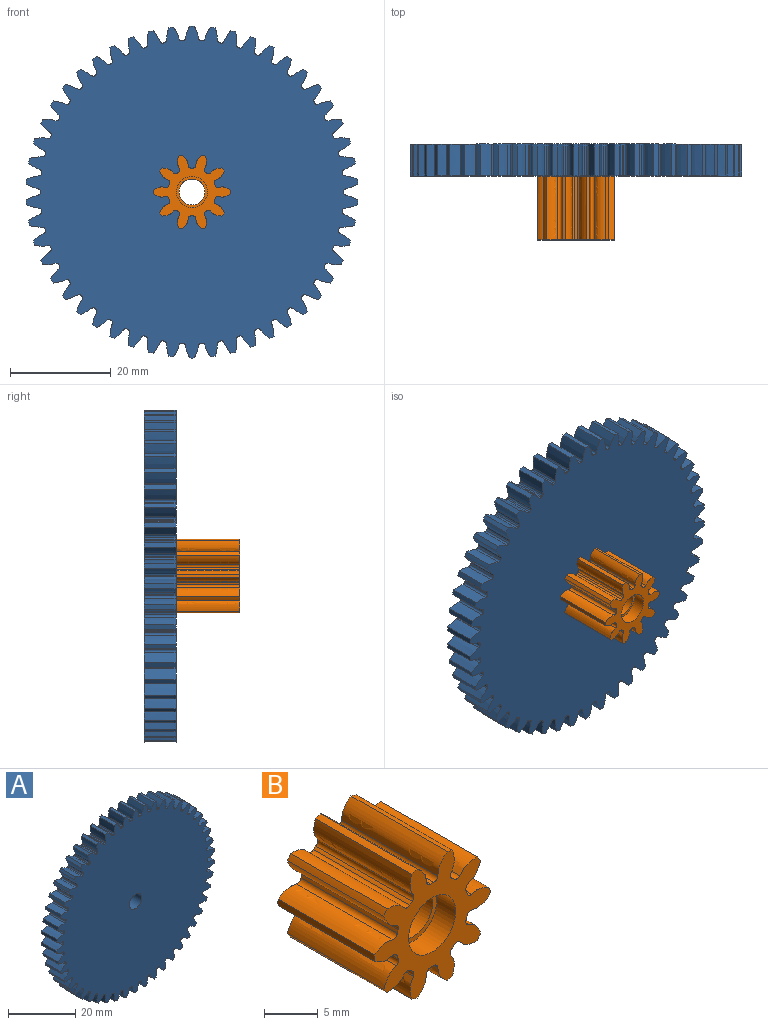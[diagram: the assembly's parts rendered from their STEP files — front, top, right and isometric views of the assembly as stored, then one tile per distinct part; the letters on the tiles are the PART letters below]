
ASSEMBLY  parts=2 mates=1
PART A: 305 faces, bbox 66x6.4x66 mm
  f0: cylinder r=2.59mm len=5.18mm, axis (0,-1,0), area 62.7mm2, adj f50,f303
  f1: cylinder r=33.02mm len=6.35mm, axis (0,1,0), area 6.2mm2, adj f50,f52,f53,f300
  f2: cylinder r=33.02mm len=6.35mm, axis (0,1,0), area 6.2mm2, adj f50,f52,f295,f298
  f3: cylinder r=33.02mm len=6.35mm, axis (0,1,0), area 6.2mm2, adj f50,f52,f290,f293
  f4: cylinder r=33.02mm len=6.35mm, axis (0,1,0), area 6.2mm2, adj f50,f52,f285,f288
  f5: cylinder r=33.02mm len=6.35mm, axis (0,1,0), area 6.2mm2, adj f50,f52,f263,f280
  f6: cylinder r=33.02mm len=6.35mm, axis (0,1,0), area 6.2mm2, adj f50,f52,f275,f278
  f7: cylinder r=33.02mm len=6.35mm, axis (0,1,0), area 6.2mm2, adj f50,f52,f270,f283
  f8: cylinder r=33.02mm len=6.35mm, axis (0,1,0), area 6.2mm2, adj f50,f52,f265,f268
  f9: cylinder r=33.02mm len=6.35mm, axis (0,1,0), area 6.2mm2, adj f50,f52,f260,f273
  f10: cylinder r=33.02mm len=6.35mm, axis (0,1,0), area 6.2mm2, adj f50,f52,f255,f258
  f11: cylinder r=33.02mm len=6.35mm, axis (0,1,0), area 6.2mm2, adj f50,f52,f250,f253
  f12: cylinder r=33.02mm len=6.35mm, axis (0,1,0), area 6.2mm2, adj f50,f52,f245,f248
  f13: cylinder r=33.02mm len=6.35mm, axis (0,1,0), area 6.2mm2, adj f50,f52,f240,f243
  f14: cylinder r=33.02mm len=6.35mm, axis (0,1,0), area 6.2mm2, adj f50,f52,f235,f238
  f15: cylinder r=33.02mm len=6.35mm, axis (0,1,0), area 6.2mm2, adj f50,f52,f230,f233
  f16: cylinder r=33.02mm len=6.35mm, axis (0,1,0), area 6.2mm2, adj f50,f52,f225,f228
  f17: cylinder r=33.02mm len=6.35mm, axis (0,1,0), area 6.2mm2, adj f50,f52,f203,f220
  f18: cylinder r=33.02mm len=6.35mm, axis (0,1,0), area 6.2mm2, adj f50,f52,f215,f218
  f19: cylinder r=33.02mm len=6.35mm, axis (0,1,0), area 6.2mm2, adj f50,f52,f210,f223
  f20: cylinder r=33.02mm len=6.35mm, axis (0,1,0), area 6.2mm2, adj f50,f52,f205,f208
  f21: cylinder r=33.02mm len=6.35mm, axis (0,1,0), area 6.2mm2, adj f50,f52,f200,f213
  f22: cylinder r=33.02mm len=6.35mm, axis (0,1,0), area 6.2mm2, adj f50,f52,f195,f198
  f23: cylinder r=33.02mm len=6.35mm, axis (0,1,0), area 6.2mm2, adj f50,f52,f190,f193
  f24: cylinder r=33.02mm len=6.35mm, axis (0,1,0), area 6.2mm2, adj f50,f52,f185,f188
  f25: cylinder r=33.02mm len=6.35mm, axis (0,1,0), area 6.2mm2, adj f50,f52,f180,f183
  f26: cylinder r=33.02mm len=6.35mm, axis (0,1,0), area 6.2mm2, adj f50,f52,f175,f178
  f27: cylinder r=33.02mm len=6.35mm, axis (0,1,0), area 6.2mm2, adj f50,f52,f170,f173
  f28: cylinder r=33.02mm len=6.35mm, axis (0,1,0), area 6.2mm2, adj f50,f52,f165,f168
  f29: cylinder r=33.02mm len=6.35mm, axis (0,1,0), area 6.2mm2, adj f50,f52,f148,f160
  f30: cylinder r=33.02mm len=6.35mm, axis (0,1,0), area 6.2mm2, adj f50,f52,f155,f158
  f31: cylinder r=33.02mm len=6.35mm, axis (0,1,0), area 6.2mm2, adj f50,f52,f143,f150
  f32: cylinder r=33.02mm len=6.35mm, axis (0,1,0), area 6.2mm2, adj f50,f52,f145,f163
  f33: cylinder r=33.02mm len=6.35mm, axis (0,1,0), area 6.2mm2, adj f50,f52,f140,f153
  f34: cylinder r=33.02mm len=6.35mm, axis (0,1,0), area 6.2mm2, adj f50,f52,f135,f138
  f35: cylinder r=33.02mm len=6.35mm, axis (0,1,0), area 6.2mm2, adj f50,f52,f130,f133
  f36: cylinder r=33.02mm len=6.35mm, axis (0,1,0), area 6.2mm2, adj f50,f52,f125,f128
  f37: cylinder r=33.02mm len=6.35mm, axis (0,1,0), area 6.2mm2, adj f50,f52,f120,f123
  f38: cylinder r=33.02mm len=6.35mm, axis (0,1,0), area 6.2mm2, adj f50,f52,f115,f118
  f39: cylinder r=33.02mm len=6.35mm, axis (0,1,0), area 6.2mm2, adj f50,f52,f110,f113
  f40: cylinder r=33.02mm len=6.35mm, axis (0,1,0), area 6.2mm2, adj f50,f52,f105,f108
  f41: cylinder r=33.02mm len=6.35mm, axis (0,1,0), area 6.2mm2, adj f50,f52,f93,f100
  f42: cylinder r=33.02mm len=6.35mm, axis (0,1,0), area 6.2mm2, adj f50,f52,f88,f95
  f43: cylinder r=33.02mm len=6.35mm, axis (0,1,0), area 6.2mm2, adj f50,f52,f83,f90
  f44: cylinder r=33.02mm len=6.35mm, axis (0,1,0), area 6.2mm2, adj f50,f52,f68,f85
  f45: cylinder r=33.02mm len=6.35mm, axis (0,1,0), area 6.2mm2, adj f50,f52,f80,f103
  f46: cylinder r=33.02mm len=6.35mm, axis (0,1,0), area 6.2mm2, adj f50,f52,f75,f78
  f47: cylinder r=33.02mm len=6.35mm, axis (0,1,0), area 6.2mm2, adj f50,f52,f63,f70
  f48: cylinder r=33.02mm len=6.35mm, axis (0,1,0), area 6.2mm2, adj f50,f52,f65,f73
  f49: cylinder r=33.02mm len=6.35mm, axis (0,1,0), area 6.2mm2, adj f50,f52,f60,f98
  f50: plane 66.04x65.97mm, normal (0,-1,0), area 3128.1mm2, adj f0,f1,f2,f3,f4,f5,f6,f7
  f51: cylinder r=33.02mm len=6.35mm, axis (0,1,0), area 6.2mm2, adj f50,f52,f55,f58
  f52: plane 66.04x65.97mm, normal (0,1,0), area 3119mm2, adj f1,f2,f3,f4,f5,f6,f7,f8
  f53: extruded ~6.35x2.48mm, area 17mm2, adj f1,f50,f52,f56
  f54: cylinder r=30.16mm len=6.35mm, axis (0,1,0), area 2.2mm2, adj f50,f52,f56,f57
  f55: extruded ~6.35x2.48mm, area 17mm2, adj f50,f51,f52,f57
  f56: cylinder r=0.44mm len=6.35mm, axis (0,1,0), area 3.8mm2, adj f50,f52,f53,f54
  f57: cylinder r=0.44mm len=6.35mm, axis (0,1,0), area 3.8mm2, adj f50,f52,f54,f55
  f58: extruded ~6.35x2.58mm, area 17mm2, adj f50,f51,f52,f61
  f59: cylinder r=30.16mm len=6.35mm, axis (0,1,0), area 2.2mm2, adj f50,f52,f61,f62
  f60: extruded ~6.35x2.34mm, area 17mm2, adj f49,f50,f52,f62
  f61: cylinder r=0.44mm len=6.35mm, axis (0,1,0), area 3.8mm2, adj f50,f52,f58,f59
  f62: cylinder r=0.44mm len=6.35mm, axis (0,1,0), area 3.8mm2, adj f50,f52,f59,f60
  f63: extruded ~6.35x2.34mm, area 17mm2, adj f47,f50,f52,f66
  f64: cylinder r=30.16mm len=6.35mm, axis (0,1,0), area 2.2mm2, adj f50,f52,f66,f67
  f65: extruded ~6.35x2.54mm, area 17mm2, adj f48,f50,f52,f67
  f66: cylinder r=0.44mm len=6.35mm, axis (0,1,0), area 3.8mm2, adj f50,f52,f63,f64
  f67: cylinder r=0.44mm len=6.35mm, axis (0,1,0), area 3.8mm2, adj f50,f52,f64,f65
  f68: extruded ~6.35x2.48mm, area 17mm2, adj f44,f50,f52,f71
  f69: cylinder r=30.16mm len=6.35mm, axis (0,1,0), area 2.2mm2, adj f50,f52,f71,f72
  f70: extruded ~6.35x2.42mm, area 17mm2, adj f47,f50,f52,f72
  f71: cylinder r=0.44mm len=6.35mm, axis (0,1,0), area 3.8mm2, adj f50,f52,f68,f69
  f72: cylinder r=0.44mm len=6.35mm, axis (0,1,0), area 3.8mm2, adj f50,f52,f69,f70
  f73: extruded ~6.35x2.16mm, area 17mm2, adj f48,f50,f52,f76
  f74: cylinder r=30.16mm len=6.35mm, axis (0,1,0), area 2.2mm2, adj f50,f52,f76,f77
  f75: extruded ~6.35x2.62mm, area 17mm2, adj f46,f50,f52,f77
  f76: cylinder r=0.44mm len=6.35mm, axis (0,1,0), area 3.8mm2, adj f50,f52,f73,f74
  f77: cylinder r=0.44mm len=6.35mm, axis (0,1,0), area 3.8mm2, adj f50,f52,f74,f75
  f78: extruded ~6.35x1.95mm, area 17mm2, adj f46,f50,f52,f81
  f79: cylinder r=30.16mm len=6.35mm, axis (0,1,0), area 2.2mm2, adj f50,f52,f81,f82
  f80: extruded ~6.35x2.66mm, area 17mm2, adj f45,f50,f52,f82
  f81: cylinder r=0.44mm len=6.35mm, axis (0,1,0), area 3.8mm2, adj f50,f52,f78,f79
  f82: cylinder r=0.44mm len=6.35mm, axis (0,1,0), area 3.8mm2, adj f50,f52,f79,f80
  f83: extruded ~6.35x2.59mm, area 17mm2, adj f43,f50,f52,f86
  f84: cylinder r=30.16mm len=6.35mm, axis (0,1,0), area 2.2mm2, adj f50,f52,f86,f87
  f85: extruded ~6.35x2.25mm, area 17mm2, adj f44,f50,f52,f87
  f86: cylinder r=0.44mm len=6.35mm, axis (0,1,0), area 3.8mm2, adj f50,f52,f83,f84
  f87: cylinder r=0.44mm len=6.35mm, axis (0,1,0), area 3.8mm2, adj f50,f52,f84,f85
  f88: extruded ~6.35x2.65mm, area 17mm2, adj f42,f50,f52,f91
  f89: cylinder r=30.16mm len=6.35mm, axis (0,1,0), area 2.2mm2, adj f50,f52,f91,f92
  f90: extruded ~6.35x2.06mm, area 17mm2, adj f43,f50,f52,f92
  f91: cylinder r=0.44mm len=6.35mm, axis (0,1,0), area 3.8mm2, adj f50,f52,f88,f89
  f92: cylinder r=0.44mm len=6.35mm, axis (0,1,0), area 3.8mm2, adj f50,f52,f89,f90
  f93: extruded ~6.35x2.67mm, area 17mm2, adj f41,f50,f52,f96
  f94: cylinder r=30.16mm len=6.35mm, axis (0,1,0), area 2.2mm2, adj f50,f52,f96,f97
  f95: extruded ~6.35x1.94mm, area 17mm2, adj f42,f50,f52,f97
  f96: cylinder r=0.44mm len=6.35mm, axis (0,1,0), area 3.8mm2, adj f50,f52,f93,f94
  f97: cylinder r=0.44mm len=6.35mm, axis (0,1,0), area 3.8mm2, adj f50,f52,f94,f95
  f98: extruded ~6.35x2.65mm, area 17mm2, adj f49,f50,f52,f101
  f99: cylinder r=30.16mm len=6.35mm, axis (0,1,0), area 2.2mm2, adj f50,f52,f101,f102
  f100: extruded ~6.35x2.16mm, area 17mm2, adj f41,f50,f52,f102
  f101: cylinder r=0.44mm len=6.35mm, axis (0,1,0), area 3.8mm2, adj f50,f52,f98,f99
  f102: cylinder r=0.44mm len=6.35mm, axis (0,1,0), area 3.8mm2, adj f50,f52,f99,f100
  f103: extruded ~6.35x2.06mm, area 17mm2, adj f45,f50,f52,f106
  f104: cylinder r=30.16mm len=6.35mm, axis (0,1,0), area 2.2mm2, adj f50,f52,f106,f107
  f105: extruded ~6.35x2.66mm, area 17mm2, adj f40,f50,f52,f107
  f106: cylinder r=0.44mm len=6.35mm, axis (0,1,0), area 3.8mm2, adj f50,f52,f103,f104
  f107: cylinder r=0.44mm len=6.35mm, axis (0,1,0), area 3.8mm2, adj f50,f52,f104,f105
  f108: extruded ~6.35x2.25mm, area 17mm2, adj f40,f50,f52,f111
  f109: cylinder r=30.16mm len=6.35mm, axis (0,1,0), area 2.2mm2, adj f50,f52,f111,f112
  f110: extruded ~6.35x2.62mm, area 17mm2, adj f39,f50,f52,f112
  f111: cylinder r=0.44mm len=6.35mm, axis (0,1,0), area 3.8mm2, adj f50,f52,f108,f109
  f112: cylinder r=0.44mm len=6.35mm, axis (0,1,0), area 3.8mm2, adj f50,f52,f109,f110
  f113: extruded ~6.35x2.41mm, area 17mm2, adj f39,f50,f52,f116
  f114: cylinder r=30.16mm len=6.35mm, axis (0,1,0), area 2.2mm2, adj f50,f52,f116,f117
  f115: extruded ~6.35x2.54mm, area 17mm2, adj f38,f50,f52,f117
  f116: cylinder r=0.44mm len=6.35mm, axis (0,1,0), area 3.8mm2, adj f50,f52,f113,f114
  f117: cylinder r=0.44mm len=6.35mm, axis (0,1,0), area 3.8mm2, adj f50,f52,f114,f115
  f118: extruded ~6.35x2.54mm, area 17mm2, adj f38,f50,f52,f121
  f119: cylinder r=30.16mm len=6.35mm, axis (0,1,0), area 2.2mm2, adj f50,f52,f121,f122
  f120: extruded ~6.35x2.41mm, area 17mm2, adj f37,f50,f52,f122
  f121: cylinder r=0.44mm len=6.35mm, axis (0,1,0), area 3.8mm2, adj f50,f52,f118,f119
  f122: cylinder r=0.44mm len=6.35mm, axis (0,1,0), area 3.8mm2, adj f50,f52,f119,f120
  f123: extruded ~6.35x2.62mm, area 17mm2, adj f37,f50,f52,f126
  f124: cylinder r=30.16mm len=6.35mm, axis (0,1,0), area 2.2mm2, adj f50,f52,f126,f127
  f125: extruded ~6.35x2.25mm, area 17mm2, adj f36,f50,f52,f127
  f126: cylinder r=0.44mm len=6.35mm, axis (0,1,0), area 3.8mm2, adj f50,f52,f123,f124
  f127: cylinder r=0.44mm len=6.35mm, axis (0,1,0), area 3.8mm2, adj f50,f52,f124,f125
  f128: extruded ~6.35x2.66mm, area 17mm2, adj f36,f50,f52,f131
  f129: cylinder r=30.16mm len=6.35mm, axis (0,1,0), area 2.2mm2, adj f50,f52,f131,f132
  f130: extruded ~6.35x2.06mm, area 17mm2, adj f35,f50,f52,f132
  f131: cylinder r=0.44mm len=6.35mm, axis (0,1,0), area 3.8mm2, adj f50,f52,f128,f129
  f132: cylinder r=0.44mm len=6.35mm, axis (0,1,0), area 3.8mm2, adj f50,f52,f129,f130
  f133: extruded ~6.35x2.66mm, area 17mm2, adj f35,f50,f52,f136
  f134: cylinder r=30.16mm len=6.35mm, axis (0,1,0), area 2.2mm2, adj f50,f52,f136,f137
  f135: extruded ~6.35x1.95mm, area 17mm2, adj f34,f50,f52,f137
  f136: cylinder r=0.44mm len=6.35mm, axis (0,1,0), area 3.8mm2, adj f50,f52,f133,f134
  f137: cylinder r=0.44mm len=6.35mm, axis (0,1,0), area 3.8mm2, adj f50,f52,f134,f135
  f138: extruded ~6.35x2.62mm, area 17mm2, adj f34,f50,f52,f141
  f139: cylinder r=30.16mm len=6.35mm, axis (0,1,0), area 2.2mm2, adj f50,f52,f141,f142
  f140: extruded ~6.35x2.16mm, area 17mm2, adj f33,f50,f52,f142
  f141: cylinder r=0.44mm len=6.35mm, axis (0,1,0), area 3.8mm2, adj f50,f52,f138,f139
  f142: cylinder r=0.44mm len=6.35mm, axis (0,1,0), area 3.8mm2, adj f50,f52,f139,f140
  f143: extruded ~6.35x2.06mm, area 17mm2, adj f31,f50,f52,f146
  f144: cylinder r=30.16mm len=6.35mm, axis (0,1,0), area 2.2mm2, adj f50,f52,f146,f147
  f145: extruded ~6.35x2.65mm, area 17mm2, adj f32,f50,f52,f147
  f146: cylinder r=0.44mm len=6.35mm, axis (0,1,0), area 3.8mm2, adj f50,f52,f143,f144
  f147: cylinder r=0.44mm len=6.35mm, axis (0,1,0), area 3.8mm2, adj f50,f52,f144,f145
  f148: extruded ~6.35x2.25mm, area 17mm2, adj f29,f50,f52,f151
  f149: cylinder r=30.16mm len=6.35mm, axis (0,1,0), area 2.2mm2, adj f50,f52,f151,f152
  f150: extruded ~6.35x2.59mm, area 17mm2, adj f31,f50,f52,f152
  f151: cylinder r=0.44mm len=6.35mm, axis (0,1,0), area 3.8mm2, adj f50,f52,f148,f149
  f152: cylinder r=0.44mm len=6.35mm, axis (0,1,0), area 3.8mm2, adj f50,f52,f149,f150
  f153: extruded ~6.35x2.54mm, area 17mm2, adj f33,f50,f52,f156
  f154: cylinder r=30.16mm len=6.35mm, axis (0,1,0), area 2.2mm2, adj f50,f52,f156,f157
  f155: extruded ~6.35x2.34mm, area 17mm2, adj f30,f50,f52,f157
  f156: cylinder r=0.44mm len=6.35mm, axis (0,1,0), area 3.8mm2, adj f50,f52,f153,f154
  f157: cylinder r=0.44mm len=6.35mm, axis (0,1,0), area 3.8mm2, adj f50,f52,f154,f155
  f158: extruded ~6.35x2.42mm, area 17mm2, adj f30,f50,f52,f161
  f159: cylinder r=30.16mm len=6.35mm, axis (0,1,0), area 2.2mm2, adj f50,f52,f161,f162
  f160: extruded ~6.35x2.48mm, area 17mm2, adj f29,f50,f52,f162
  f161: cylinder r=0.44mm len=6.35mm, axis (0,1,0), area 3.8mm2, adj f50,f52,f158,f159
  f162: cylinder r=0.44mm len=6.35mm, axis (0,1,0), area 3.8mm2, adj f50,f52,f159,f160
  f163: extruded ~6.35x1.94mm, area 17mm2, adj f32,f50,f52,f166
  f164: cylinder r=30.16mm len=6.35mm, axis (0,1,0), area 2.2mm2, adj f50,f52,f166,f167
  f165: extruded ~6.35x2.67mm, area 17mm2, adj f28,f50,f52,f167
  f166: cylinder r=0.44mm len=6.35mm, axis (0,1,0), area 3.8mm2, adj f50,f52,f163,f164
  f167: cylinder r=0.44mm len=6.35mm, axis (0,1,0), area 3.8mm2, adj f50,f52,f164,f165
  f168: extruded ~6.35x2.16mm, area 17mm2, adj f28,f50,f52,f171
  f169: cylinder r=30.16mm len=6.35mm, axis (0,1,0), area 2.2mm2, adj f50,f52,f171,f172
  f170: extruded ~6.35x2.65mm, area 17mm2, adj f27,f50,f52,f172
  f171: cylinder r=0.44mm len=6.35mm, axis (0,1,0), area 3.8mm2, adj f50,f52,f168,f169
  f172: cylinder r=0.44mm len=6.35mm, axis (0,1,0), area 3.8mm2, adj f50,f52,f169,f170
  f173: extruded ~6.35x2.34mm, area 17mm2, adj f27,f50,f52,f176
  f174: cylinder r=30.16mm len=6.35mm, axis (0,1,0), area 2.2mm2, adj f50,f52,f176,f177
  f175: extruded ~6.35x2.58mm, area 17mm2, adj f26,f50,f52,f177
  f176: cylinder r=0.44mm len=6.35mm, axis (0,1,0), area 3.8mm2, adj f50,f52,f173,f174
  f177: cylinder r=0.44mm len=6.35mm, axis (0,1,0), area 3.8mm2, adj f50,f52,f174,f175
  f178: extruded ~6.35x2.48mm, area 17mm2, adj f26,f50,f52,f181
  f179: cylinder r=30.16mm len=6.35mm, axis (0,1,0), area 2.2mm2, adj f50,f52,f181,f182
  f180: extruded ~6.35x2.48mm, area 17mm2, adj f25,f50,f52,f182
  f181: cylinder r=0.44mm len=6.35mm, axis (0,1,0), area 3.8mm2, adj f50,f52,f178,f179
  f182: cylinder r=0.44mm len=6.35mm, axis (0,1,0), area 3.8mm2, adj f50,f52,f179,f180
  f183: extruded ~6.35x2.58mm, area 17mm2, adj f25,f50,f52,f186
  f184: cylinder r=30.16mm len=6.35mm, axis (0,1,0), area 2.2mm2, adj f50,f52,f186,f187
  f185: extruded ~6.35x2.34mm, area 17mm2, adj f24,f50,f52,f187
  f186: cylinder r=0.44mm len=6.35mm, axis (0,1,0), area 3.8mm2, adj f50,f52,f183,f184
  f187: cylinder r=0.44mm len=6.35mm, axis (0,1,0), area 3.8mm2, adj f50,f52,f184,f185
  f188: extruded ~6.35x2.65mm, area 17mm2, adj f24,f50,f52,f191
  f189: cylinder r=30.16mm len=6.35mm, axis (0,1,0), area 2.2mm2, adj f50,f52,f191,f192
  f190: extruded ~6.35x2.16mm, area 17mm2, adj f23,f50,f52,f192
  f191: cylinder r=0.44mm len=6.35mm, axis (0,1,0), area 3.8mm2, adj f50,f52,f188,f189
  f192: cylinder r=0.44mm len=6.35mm, axis (0,1,0), area 3.8mm2, adj f50,f52,f189,f190
  f193: extruded ~6.35x2.67mm, area 17mm2, adj f23,f50,f52,f196
  f194: cylinder r=30.16mm len=6.35mm, axis (0,1,0), area 2.2mm2, adj f50,f52,f196,f197
  f195: extruded ~6.35x1.94mm, area 17mm2, adj f22,f50,f52,f197
  f196: cylinder r=0.44mm len=6.35mm, axis (0,1,0), area 3.8mm2, adj f50,f52,f193,f194
  f197: cylinder r=0.44mm len=6.35mm, axis (0,1,0), area 3.8mm2, adj f50,f52,f194,f195
  f198: extruded ~6.35x2.65mm, area 17mm2, adj f22,f50,f52,f201
  f199: cylinder r=30.16mm len=6.35mm, axis (0,1,0), area 2.2mm2, adj f50,f52,f201,f202
  f200: extruded ~6.35x2.06mm, area 17mm2, adj f21,f50,f52,f202
  f201: cylinder r=0.44mm len=6.35mm, axis (0,1,0), area 3.8mm2, adj f50,f52,f198,f199
  f202: cylinder r=0.44mm len=6.35mm, axis (0,1,0), area 3.8mm2, adj f50,f52,f199,f200
  f203: extruded ~6.35x2.34mm, area 17mm2, adj f17,f50,f52,f206
  f204: cylinder r=30.16mm len=6.35mm, axis (0,1,0), area 2.2mm2, adj f50,f52,f206,f207
  f205: extruded ~6.35x2.54mm, area 17mm2, adj f20,f50,f52,f207
  f206: cylinder r=0.44mm len=6.35mm, axis (0,1,0), area 3.8mm2, adj f50,f52,f203,f204
  f207: cylinder r=0.44mm len=6.35mm, axis (0,1,0), area 3.8mm2, adj f50,f52,f204,f205
  f208: extruded ~6.35x2.16mm, area 17mm2, adj f20,f50,f52,f211
  f209: cylinder r=30.16mm len=6.35mm, axis (0,1,0), area 2.2mm2, adj f50,f52,f211,f212
  f210: extruded ~6.35x2.62mm, area 17mm2, adj f19,f50,f52,f212
  f211: cylinder r=0.44mm len=6.35mm, axis (0,1,0), area 3.8mm2, adj f50,f52,f208,f209
  f212: cylinder r=0.44mm len=6.35mm, axis (0,1,0), area 3.8mm2, adj f50,f52,f209,f210
  f213: extruded ~6.35x2.59mm, area 17mm2, adj f21,f50,f52,f216
  f214: cylinder r=30.16mm len=6.35mm, axis (0,1,0), area 2.2mm2, adj f50,f52,f216,f217
  f215: extruded ~6.35x2.25mm, area 17mm2, adj f18,f50,f52,f217
  f216: cylinder r=0.44mm len=6.35mm, axis (0,1,0), area 3.8mm2, adj f50,f52,f213,f214
  f217: cylinder r=0.44mm len=6.35mm, axis (0,1,0), area 3.8mm2, adj f50,f52,f214,f215
  f218: extruded ~6.35x2.48mm, area 17mm2, adj f18,f50,f52,f221
  f219: cylinder r=30.16mm len=6.35mm, axis (0,1,0), area 2.2mm2, adj f50,f52,f221,f222
  f220: extruded ~6.35x2.42mm, area 17mm2, adj f17,f50,f52,f222
  f221: cylinder r=0.44mm len=6.35mm, axis (0,1,0), area 3.8mm2, adj f50,f52,f218,f219
  f222: cylinder r=0.44mm len=6.35mm, axis (0,1,0), area 3.8mm2, adj f50,f52,f219,f220
  f223: extruded ~6.35x1.95mm, area 17mm2, adj f19,f50,f52,f226
  f224: cylinder r=30.16mm len=6.35mm, axis (0,1,0), area 2.2mm2, adj f50,f52,f226,f227
  f225: extruded ~6.35x2.66mm, area 17mm2, adj f16,f50,f52,f227
  f226: cylinder r=0.44mm len=6.35mm, axis (0,1,0), area 3.8mm2, adj f50,f52,f223,f224
  f227: cylinder r=0.44mm len=6.35mm, axis (0,1,0), area 3.8mm2, adj f50,f52,f224,f225
  f228: extruded ~6.35x2.06mm, area 17mm2, adj f16,f50,f52,f231
  f229: cylinder r=30.16mm len=6.35mm, axis (0,1,0), area 2.2mm2, adj f50,f52,f231,f232
  f230: extruded ~6.35x2.66mm, area 17mm2, adj f15,f50,f52,f232
  f231: cylinder r=0.44mm len=6.35mm, axis (0,1,0), area 3.8mm2, adj f50,f52,f228,f229
  f232: cylinder r=0.44mm len=6.35mm, axis (0,1,0), area 3.8mm2, adj f50,f52,f229,f230
  f233: extruded ~6.35x2.25mm, area 17mm2, adj f15,f50,f52,f236
  f234: cylinder r=30.16mm len=6.35mm, axis (0,1,0), area 2.2mm2, adj f50,f52,f236,f237
  f235: extruded ~6.35x2.62mm, area 17mm2, adj f14,f50,f52,f237
  f236: cylinder r=0.44mm len=6.35mm, axis (0,1,0), area 3.8mm2, adj f50,f52,f233,f234
  f237: cylinder r=0.44mm len=6.35mm, axis (0,1,0), area 3.8mm2, adj f50,f52,f234,f235
  f238: extruded ~6.35x2.41mm, area 17mm2, adj f14,f50,f52,f241
  f239: cylinder r=30.16mm len=6.35mm, axis (0,1,0), area 2.2mm2, adj f50,f52,f241,f242
  f240: extruded ~6.35x2.54mm, area 17mm2, adj f13,f50,f52,f242
  f241: cylinder r=0.44mm len=6.35mm, axis (0,1,0), area 3.8mm2, adj f50,f52,f238,f239
  f242: cylinder r=0.44mm len=6.35mm, axis (0,1,0), area 3.8mm2, adj f50,f52,f239,f240
  f243: extruded ~6.35x2.54mm, area 17mm2, adj f13,f50,f52,f246
  f244: cylinder r=30.16mm len=6.35mm, axis (0,1,0), area 2.2mm2, adj f50,f52,f246,f247
  f245: extruded ~6.35x2.41mm, area 17mm2, adj f12,f50,f52,f247
  f246: cylinder r=0.44mm len=6.35mm, axis (0,1,0), area 3.8mm2, adj f50,f52,f243,f244
  f247: cylinder r=0.44mm len=6.35mm, axis (0,1,0), area 3.8mm2, adj f50,f52,f244,f245
  f248: extruded ~6.35x2.62mm, area 17mm2, adj f12,f50,f52,f251
  f249: cylinder r=30.16mm len=6.35mm, axis (0,1,0), area 2.2mm2, adj f50,f52,f251,f252
  f250: extruded ~6.35x2.25mm, area 17mm2, adj f11,f50,f52,f252
  f251: cylinder r=0.44mm len=6.35mm, axis (0,1,0), area 3.8mm2, adj f50,f52,f248,f249
  f252: cylinder r=0.44mm len=6.35mm, axis (0,1,0), area 3.8mm2, adj f50,f52,f249,f250
  f253: extruded ~6.35x2.66mm, area 17mm2, adj f11,f50,f52,f256
  f254: cylinder r=30.16mm len=6.35mm, axis (0,1,0), area 2.2mm2, adj f50,f52,f256,f257
  f255: extruded ~6.35x2.06mm, area 17mm2, adj f10,f50,f52,f257
  f256: cylinder r=0.44mm len=6.35mm, axis (0,1,0), area 3.8mm2, adj f50,f52,f253,f254
  f257: cylinder r=0.44mm len=6.35mm, axis (0,1,0), area 3.8mm2, adj f50,f52,f254,f255
  f258: extruded ~6.35x2.66mm, area 17mm2, adj f10,f50,f52,f261
  f259: cylinder r=30.16mm len=6.35mm, axis (0,1,0), area 2.2mm2, adj f50,f52,f261,f262
  f260: extruded ~6.35x1.95mm, area 17mm2, adj f9,f50,f52,f262
  f261: cylinder r=0.44mm len=6.35mm, axis (0,1,0), area 3.8mm2, adj f50,f52,f258,f259
  f262: cylinder r=0.44mm len=6.35mm, axis (0,1,0), area 3.8mm2, adj f50,f52,f259,f260
  f263: extruded ~6.35x2.42mm, area 17mm2, adj f5,f50,f52,f266
  f264: cylinder r=30.16mm len=6.35mm, axis (0,1,0), area 2.2mm2, adj f50,f52,f266,f267
  f265: extruded ~6.35x2.48mm, area 17mm2, adj f8,f50,f52,f267
  f266: cylinder r=0.44mm len=6.35mm, axis (0,1,0), area 3.8mm2, adj f50,f52,f263,f264
  f267: cylinder r=0.44mm len=6.35mm, axis (0,1,0), area 3.8mm2, adj f50,f52,f264,f265
  f268: extruded ~6.35x2.25mm, area 17mm2, adj f8,f50,f52,f271
  f269: cylinder r=30.16mm len=6.35mm, axis (0,1,0), area 2.2mm2, adj f50,f52,f271,f272
  f270: extruded ~6.35x2.59mm, area 17mm2, adj f7,f50,f52,f272
  f271: cylinder r=0.44mm len=6.35mm, axis (0,1,0), area 3.8mm2, adj f50,f52,f268,f269
  f272: cylinder r=0.44mm len=6.35mm, axis (0,1,0), area 3.8mm2, adj f50,f52,f269,f270
  f273: extruded ~6.35x2.62mm, area 17mm2, adj f9,f50,f52,f276
  f274: cylinder r=30.16mm len=6.35mm, axis (0,1,0), area 2.2mm2, adj f50,f52,f276,f277
  f275: extruded ~6.35x2.16mm, area 17mm2, adj f6,f50,f52,f277
  f276: cylinder r=0.44mm len=6.35mm, axis (0,1,0), area 3.8mm2, adj f50,f52,f273,f274
  f277: cylinder r=0.44mm len=6.35mm, axis (0,1,0), area 3.8mm2, adj f50,f52,f274,f275
  f278: extruded ~6.35x2.54mm, area 17mm2, adj f6,f50,f52,f281
  f279: cylinder r=30.16mm len=6.35mm, axis (0,1,0), area 2.2mm2, adj f50,f52,f281,f282
  f280: extruded ~6.35x2.34mm, area 17mm2, adj f5,f50,f52,f282
  f281: cylinder r=0.44mm len=6.35mm, axis (0,1,0), area 3.8mm2, adj f50,f52,f278,f279
  f282: cylinder r=0.44mm len=6.35mm, axis (0,1,0), area 3.8mm2, adj f50,f52,f279,f280
  f283: extruded ~6.35x2.06mm, area 17mm2, adj f7,f50,f52,f286
  f284: cylinder r=30.16mm len=6.35mm, axis (0,1,0), area 2.2mm2, adj f50,f52,f286,f287
  f285: extruded ~6.35x2.65mm, area 17mm2, adj f4,f50,f52,f287
  f286: cylinder r=0.44mm len=6.35mm, axis (0,1,0), area 3.8mm2, adj f50,f52,f283,f284
  f287: cylinder r=0.44mm len=6.35mm, axis (0,1,0), area 3.8mm2, adj f50,f52,f284,f285
  f288: extruded ~6.35x1.94mm, area 17mm2, adj f4,f50,f52,f291
  f289: cylinder r=30.16mm len=6.35mm, axis (0,1,0), area 2.2mm2, adj f50,f52,f291,f292
  f290: extruded ~6.35x2.67mm, area 17mm2, adj f3,f50,f52,f292
  f291: cylinder r=0.44mm len=6.35mm, axis (0,1,0), area 3.8mm2, adj f50,f52,f288,f289
  f292: cylinder r=0.44mm len=6.35mm, axis (0,1,0), area 3.8mm2, adj f50,f52,f289,f290
  f293: extruded ~6.35x2.16mm, area 17mm2, adj f3,f50,f52,f296
  f294: cylinder r=30.16mm len=6.35mm, axis (0,1,0), area 2.2mm2, adj f50,f52,f296,f297
  f295: extruded ~6.35x2.65mm, area 17mm2, adj f2,f50,f52,f297
  f296: cylinder r=0.44mm len=6.35mm, axis (0,1,0), area 3.8mm2, adj f50,f52,f293,f294
  f297: cylinder r=0.44mm len=6.35mm, axis (0,1,0), area 3.8mm2, adj f50,f52,f294,f295
  f298: extruded ~6.35x2.34mm, area 17mm2, adj f2,f50,f52,f301
  f299: cylinder r=30.16mm len=6.35mm, axis (0,1,0), area 2.2mm2, adj f50,f52,f301,f302
  f300: extruded ~6.35x2.58mm, area 17mm2, adj f1,f50,f52,f302
  f301: cylinder r=0.44mm len=6.35mm, axis (0,1,0), area 3.8mm2, adj f50,f52,f298,f299
  f302: cylinder r=0.44mm len=6.35mm, axis (0,1,0), area 3.8mm2, adj f50,f52,f299,f300
  f303: plane 6.2x6.2mm, normal (0,1,0), area 9.1mm2, adj f0,f304
  f304: cylinder r=3.1mm len=6.2mm, axis (0,1,0), area 48.7mm2, adj f52,f303
PART B: 65 faces, bbox 15.3x12.7x14.7 mm
  f0: cylinder r=2.58mm len=10.2mm, axis (0,-1,0), area 165.6mm2, adj f12,f63
  f1: cylinder r=7.62mm len=12.7mm, axis (0,1,0), area 9.5mm2, adj f10,f12,f15,f59
  f2: cylinder r=7.62mm len=12.7mm, axis (0,1,0), area 9.5mm2, adj f10,f12,f54,f60
  f3: cylinder r=7.62mm len=12.7mm, axis (0,1,0), area 9.5mm2, adj f10,f12,f45,f49
  f4: cylinder r=7.62mm len=12.7mm, axis (0,1,0), area 9.5mm2, adj f10,f12,f44,f55
  f5: cylinder r=7.62mm len=12.7mm, axis (0,1,0), area 9.5mm2, adj f10,f12,f35,f39
  f6: cylinder r=7.62mm len=12.7mm, axis (0,1,0), area 9.5mm2, adj f10,f12,f34,f50
  f7: cylinder r=7.62mm len=12.7mm, axis (0,1,0), area 9.5mm2, adj f10,f12,f29,f40
  f8: cylinder r=7.62mm len=12.7mm, axis (0,1,0), area 9.5mm2, adj f10,f12,f24,f30
  f9: cylinder r=7.62mm len=12.7mm, axis (0,1,0), area 9.5mm2, adj f10,f12,f19,f25
  f10: plane 15.27x14.74mm, normal (0,-1,0), area 91mm2, adj f1,f2,f3,f4,f5,f6,f7,f8
  f11: cylinder r=7.62mm len=12.7mm, axis (0,1,0), area 9.5mm2, adj f10,f12,f14,f20
  f12: plane 15.27x14.74mm, normal (0,1,0), area 100.2mm2, adj f0,f1,f2,f3,f4,f5,f6,f7
  f13: cylinder r=4.76mm len=12.7mm, axis (0,1,0), area 5.2mm2, adj f10,f12,f16,f17
  f14: extruded ~12.7x2.43mm, area 32.7mm2, adj f10,f11,f12,f16
  f15: extruded ~12.7x1.86mm, area 32.7mm2, adj f1,f10,f12,f17
  f16: cylinder r=0.52mm len=12.7mm, axis (0,1,0), area 9.8mm2, adj f10,f12,f13,f14
  f17: cylinder r=0.52mm len=12.7mm, axis (0,1,0), area 9.8mm2, adj f10,f12,f13,f15
  f18: cylinder r=4.76mm len=12.7mm, axis (0,1,0), area 5.2mm2, adj f10,f12,f21,f22
  f19: extruded ~12.7x1.86mm, area 32.7mm2, adj f9,f10,f12,f21
  f20: extruded ~12.7x2.43mm, area 32.7mm2, adj f10,f11,f12,f22
  f21: cylinder r=0.52mm len=12.7mm, axis (0,1,0), area 9.8mm2, adj f10,f12,f18,f19
  f22: cylinder r=0.52mm len=12.7mm, axis (0,1,0), area 9.8mm2, adj f10,f12,f18,f20
  f23: cylinder r=4.76mm len=12.7mm, axis (0,1,0), area 5.2mm2, adj f10,f12,f26,f27
  f24: extruded ~12.7x2.47mm, area 32.7mm2, adj f8,f10,f12,f26
  f25: extruded ~12.7x2.28mm, area 32.7mm2, adj f9,f10,f12,f27
  f26: cylinder r=0.52mm len=12.7mm, axis (0,1,0), area 9.8mm2, adj f10,f12,f23,f24
  f27: cylinder r=0.52mm len=12.7mm, axis (0,1,0), area 9.8mm2, adj f10,f12,f23,f25
  f28: cylinder r=4.76mm len=12.7mm, axis (0,1,0), area 5.2mm2, adj f10,f12,f31,f32
  f29: extruded ~12.7x2.15mm, area 32.7mm2, adj f7,f10,f12,f31
  f30: extruded ~12.7x2.15mm, area 32.7mm2, adj f8,f10,f12,f32
  f31: cylinder r=0.52mm len=12.7mm, axis (0,1,0), area 9.8mm2, adj f10,f12,f28,f29
  f32: cylinder r=0.52mm len=12.7mm, axis (0,1,0), area 9.8mm2, adj f10,f12,f28,f30
  f33: cylinder r=4.76mm len=12.7mm, axis (0,1,0), area 5.2mm2, adj f10,f12,f36,f37
  f34: extruded ~12.7x2.43mm, area 32.7mm2, adj f6,f10,f12,f36
  f35: extruded ~12.7x1.86mm, area 32.7mm2, adj f5,f10,f12,f37
  f36: cylinder r=0.52mm len=12.7mm, axis (0,1,0), area 9.8mm2, adj f10,f12,f33,f34
  f37: cylinder r=0.52mm len=12.7mm, axis (0,1,0), area 9.8mm2, adj f10,f12,f33,f35
  f38: cylinder r=4.76mm len=12.7mm, axis (0,1,0), area 5.2mm2, adj f10,f12,f41,f42
  f39: extruded ~12.7x2.28mm, area 32.7mm2, adj f5,f10,f12,f41
  f40: extruded ~12.7x2.47mm, area 32.7mm2, adj f7,f10,f12,f42
  f41: cylinder r=0.52mm len=12.7mm, axis (0,1,0), area 9.8mm2, adj f10,f12,f38,f39
  f42: cylinder r=0.52mm len=12.7mm, axis (0,1,0), area 9.8mm2, adj f10,f12,f38,f40
  f43: cylinder r=4.76mm len=12.7mm, axis (0,1,0), area 5.2mm2, adj f10,f12,f46,f47
  f44: extruded ~12.7x2.47mm, area 32.7mm2, adj f4,f10,f12,f46
  f45: extruded ~12.7x2.28mm, area 32.7mm2, adj f3,f10,f12,f47
  f46: cylinder r=0.52mm len=12.7mm, axis (0,1,0), area 9.8mm2, adj f10,f12,f43,f44
  f47: cylinder r=0.52mm len=12.7mm, axis (0,1,0), area 9.8mm2, adj f10,f12,f43,f45
  f48: cylinder r=4.76mm len=12.7mm, axis (0,1,0), area 5.2mm2, adj f10,f12,f51,f52
  f49: extruded ~12.7x1.86mm, area 32.7mm2, adj f3,f10,f12,f51
  f50: extruded ~12.7x2.43mm, area 32.7mm2, adj f6,f10,f12,f52
  f51: cylinder r=0.52mm len=12.7mm, axis (0,1,0), area 9.8mm2, adj f10,f12,f48,f49
  f52: cylinder r=0.52mm len=12.7mm, axis (0,1,0), area 9.8mm2, adj f10,f12,f48,f50
  f53: cylinder r=4.76mm len=12.7mm, axis (0,1,0), area 5.2mm2, adj f10,f12,f56,f57
  f54: extruded ~12.7x2.15mm, area 32.7mm2, adj f2,f10,f12,f56
  f55: extruded ~12.7x2.15mm, area 32.7mm2, adj f4,f10,f12,f57
  f56: cylinder r=0.52mm len=12.7mm, axis (0,1,0), area 9.8mm2, adj f10,f12,f53,f54
  f57: cylinder r=0.52mm len=12.7mm, axis (0,1,0), area 9.8mm2, adj f10,f12,f53,f55
  f58: cylinder r=4.76mm len=12.7mm, axis (0,1,0), area 5.2mm2, adj f10,f12,f61,f62
  f59: extruded ~12.7x2.28mm, area 32.7mm2, adj f1,f10,f12,f61
  f60: extruded ~12.7x2.47mm, area 32.7mm2, adj f2,f10,f12,f62
  f61: cylinder r=0.52mm len=12.7mm, axis (0,1,0), area 9.8mm2, adj f10,f12,f58,f59
  f62: cylinder r=0.52mm len=12.7mm, axis (0,1,0), area 9.8mm2, adj f10,f12,f58,f60
  f63: plane 6.2x6.2mm, normal (0,-1,0), area 9.2mm2, adj f0,f64
  f64: cylinder r=3.1mm len=6.2mm, axis (0,-1,0), area 48.7mm2, adj f10,f63
PLACE A at identity fixed
PLACE B t=(0,-6.35,0)mm
MATE fastened A.f1 <-> B.f1  axis (0,-1,0) through (0,-6.35,0)mm
